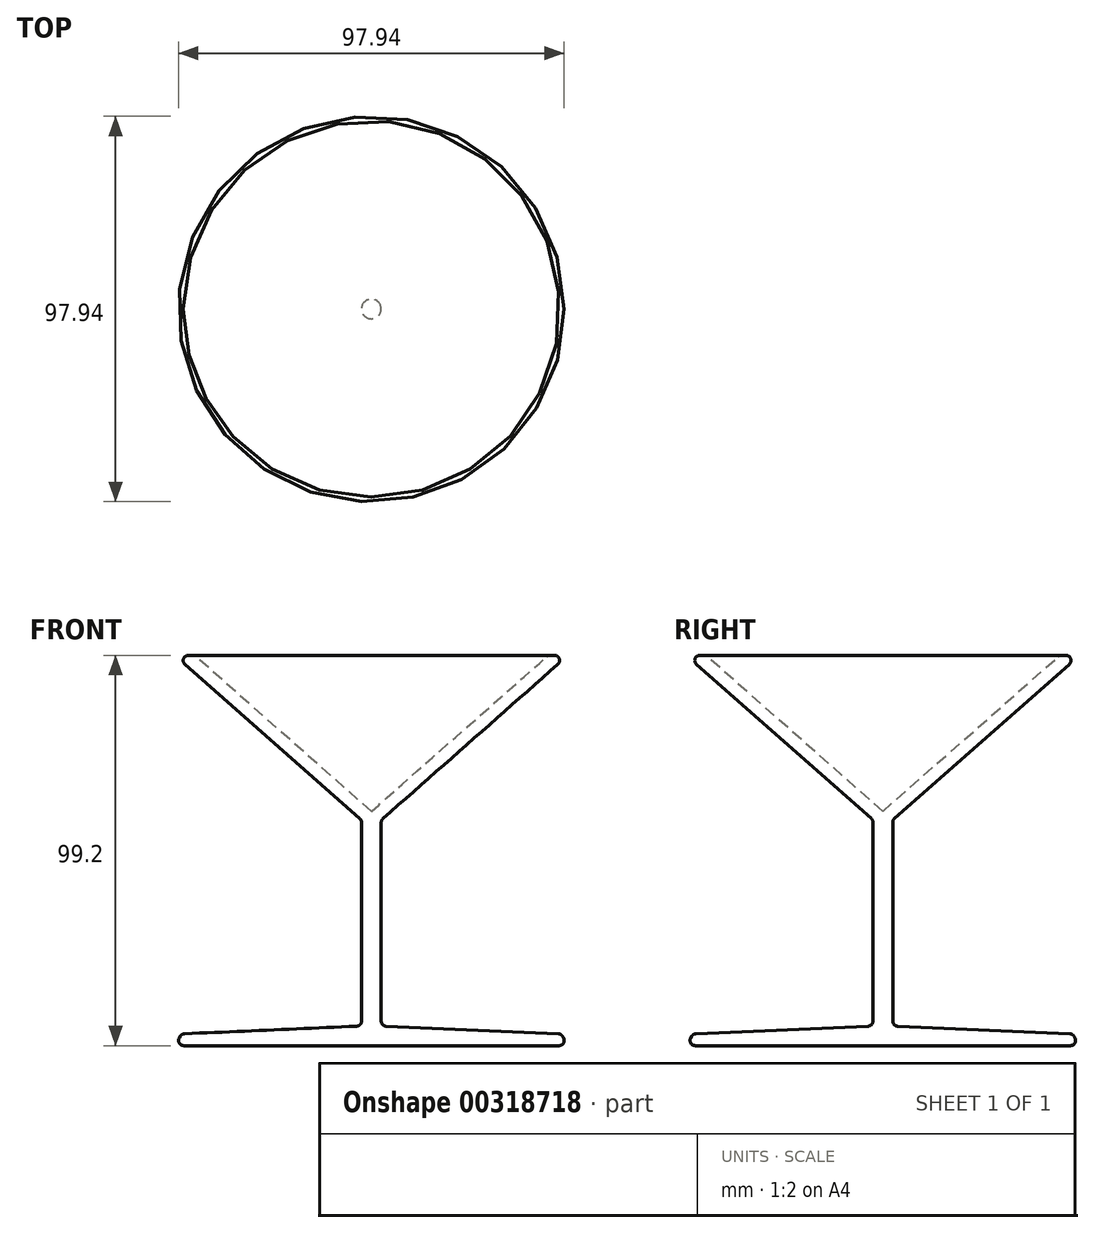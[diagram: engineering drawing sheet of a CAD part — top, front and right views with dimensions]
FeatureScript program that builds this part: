
annotation { "Feature Type Name" : "Feature", "Feature Type Description" : "" }
export const myFeature = defineFeature(function(context is Context, id is Id, definition is map)
    precondition{}
    {
        {
            var Q0;
            Q0=qCreatedBy(makeId("Front.planeOp"),FACE);
            var sketch = newSketch(context, id + "F0", { "sketchPlane" : qUnion([Q0])});
            skLineSegment(sketch, "E0", {"start": v(0, -57.31) * mm, "end": v(-50, -57.31) * mm});
            skLineSegment(sketch, "E1", {"start": v(-50, -57.31) * mm, "end": v(-48.2, -54.31) * mm});
            skLineSegment(sketch, "E2", {"start": v(-48.2, -54.31) * mm, "end": v(-2.5, -52.31) * mm});
            skLineSegment(sketch, "E3", {"start": v(-2.5, -52.31) * mm, "end": v(-2.5, 0) * mm});
            skLineSegment(sketch, "E4", {"start": v(-2.5, 0) * mm, "end": v(-50, 41.9) * mm});
            skLineSegment(sketch, "E5", {"start": v(-50, 41.9) * mm, "end": v(-45, 41.9) * mm});
            skLineSegment(sketch, "E6", {"start": v(-45, 41.9) * mm, "end": v(0, 2.2) * mm});
            skLineSegment(sketch, "E7", {"start": v(0, 2.2) * mm, "end": v(0, -57.31) * mm});
            skLineSegment(sketch, "E8", {"start": v(0, 66.27) * mm, "end": v(0, -72.97) * mm, "construction": true});
            skSolve(sketch);
        }
        {
            var Q0;
            Q0=makeQuery(id+"F0.imprint","IMPRINT",FACE,{"disambiguationData":[TD([[makeQuery(id+"F0.imprint","IMPRINT",EDGE,{"derivedFrom":sQuery(id+"F0.wireOp",EDGE,"E0")}),-1.0]])]});
            var Q1;
            Q1=sQuery(id+"F0.wireOp",EDGE,"E8");
            revolve(context, id + "F1", {"entities" : qUnion([Q0]), "axis" : qUnion([Q1]), "revolveType" : RevolveType.FULL});
        }
        {
            var Q0;
            Q0=makeQuery(id+"F1.opRevolve","SWEPT_EDGE",EDGE,{"disambiguationData":[OSD([sQuery(id+"F0.wireOp",EDGE,"E4"),sQuery(id+"F0.wireOp",EDGE,"E5")])]});
            var Q1;
            Q1=makeQuery(id+"F1.opRevolve","SWEPT_EDGE",EDGE,{"disambiguationData":[OSD([sQuery(id+"F0.wireOp",EDGE,"E5"),sQuery(id+"F0.wireOp",EDGE,"E6")])]});
            var Q2;
            Q2=makeQuery(id+"F1.opRevolve","SWEPT_EDGE",EDGE,{"disambiguationData":[OSD([sQuery(id+"F0.wireOp",EDGE,"E1"),sQuery(id+"F0.wireOp",EDGE,"E2")])]});
            var Q3;
            Q3=makeQuery(id+"F1.opRevolve","SWEPT_EDGE",EDGE,{"disambiguationData":[OSD([sQuery(id+"F0.wireOp",EDGE,"E0"),sQuery(id+"F0.wireOp",EDGE,"E1")])]});
            var Q4;
            Q4=makeQuery(id+"F1.opRevolve","SWEPT_EDGE",EDGE,{"disambiguationData":[OSD([sQuery(id+"F0.wireOp",EDGE,"E2"),sQuery(id+"F0.wireOp",EDGE,"E3")])]});
            var Q5;
            Q5=makeQuery(id+"F1.opRevolve","SWEPT_EDGE",EDGE,{"disambiguationData":[OSD([sQuery(id+"F0.wireOp",EDGE,"E3"),sQuery(id+"F0.wireOp",EDGE,"E4")])]});
            fillet(context, id + "F2", {"entities" : qUnion([Q0, Q1, Q2, Q3, Q4, Q5]), "radius" : 1.34 * mm, "tangentPropagation" : true, "allowEdgeOverflow" : false});
        }
    });
